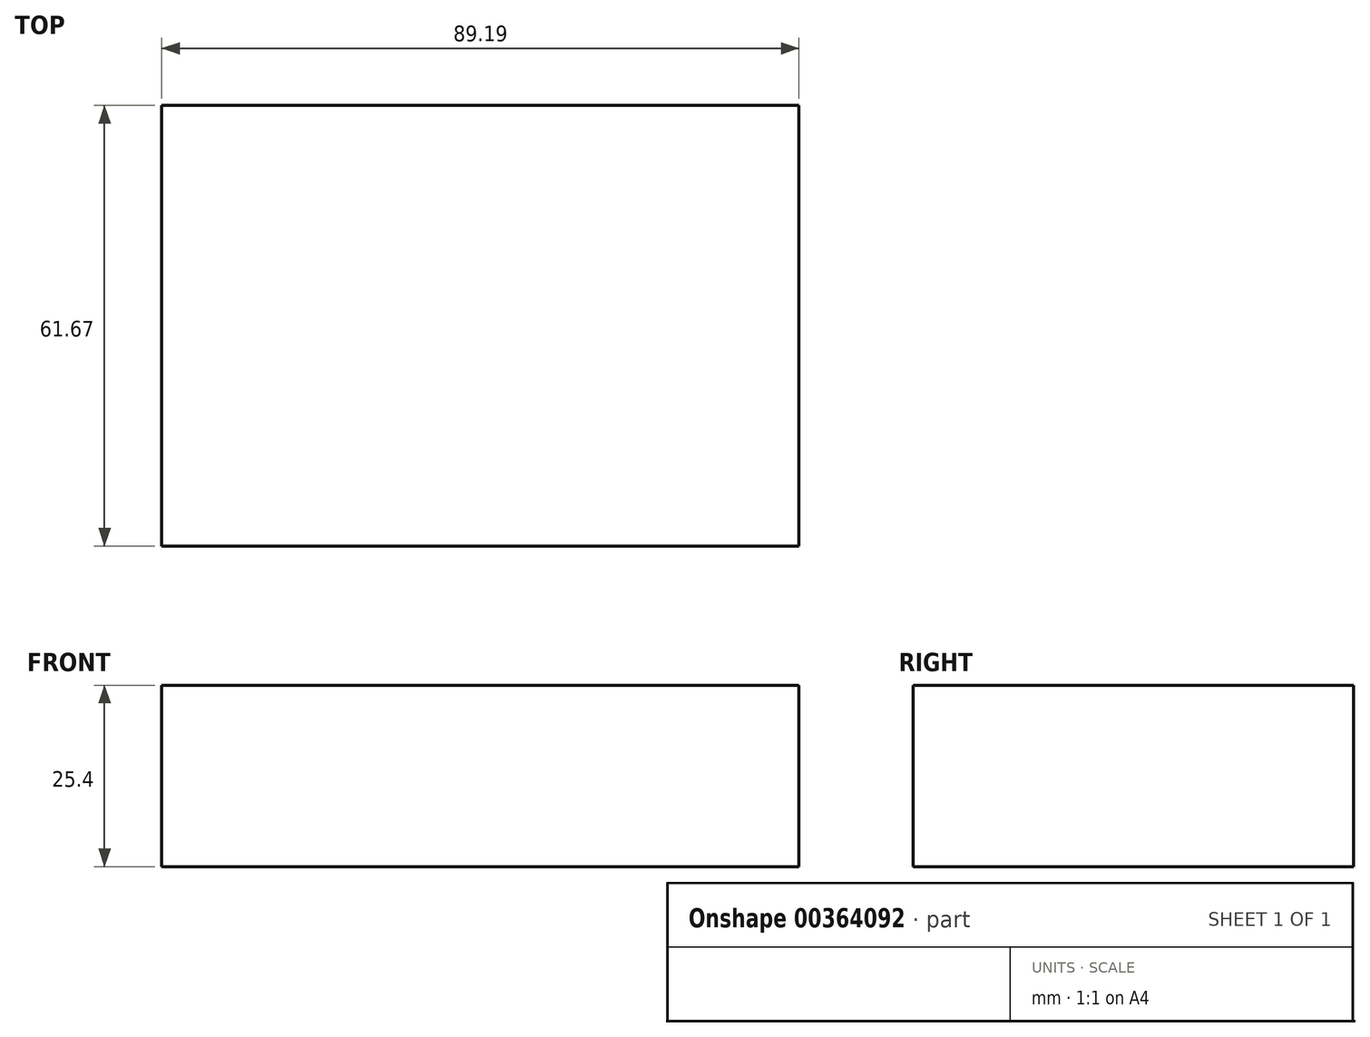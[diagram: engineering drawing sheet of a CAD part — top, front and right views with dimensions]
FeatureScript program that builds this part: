
annotation { "Feature Type Name" : "Feature", "Feature Type Description" : "" }
export const myFeature = defineFeature(function(context is Context, id is Id, definition is map)
    precondition{}
    {
        {
            var Q0;
            Q0=qCreatedBy(makeId("Top.planeOp"),FACE);
            var sketch = newSketch(context, id + "F0", { "sketchPlane" : qUnion([Q0])});
            skLineSegment(sketch, "E0.bottom", {"start": v(-113.52, -46.55) * mm, "end": v(-24.33, -46.55) * mm});
            skLineSegment(sketch, "E0.top", {"start": v(-113.52, 15.12) * mm, "end": v(-24.33, 15.12) * mm});
            skLineSegment(sketch, "E0.left", {"start": v(-113.52, -46.55) * mm, "end": v(-113.52, 15.12) * mm});
            skLineSegment(sketch, "E0.right", {"start": v(-24.33, -46.55) * mm, "end": v(-24.33, 15.12) * mm});
            skSolve(sketch);
        }
        {
            var Q0;
            Q0 = qSketchRegion(id + "F0", true);
            extrude(context, id + "F1", {"entities" : qUnion([Q0]), "depth" : 25.4 * mm});
        }
    });
